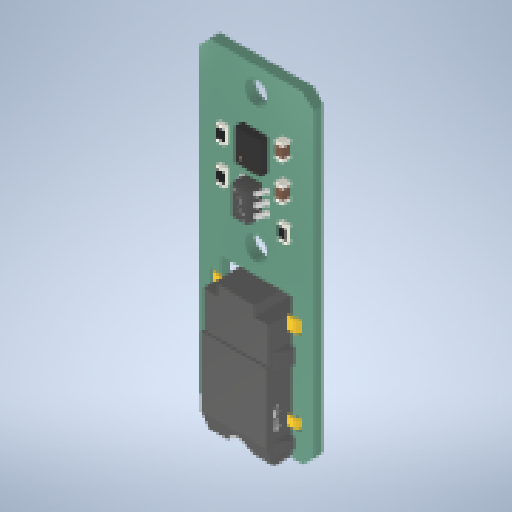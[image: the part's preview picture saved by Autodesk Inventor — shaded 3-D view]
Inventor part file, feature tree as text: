
AUTODESK INVENTOR PART (.ipt)
format: ipt  version: 2024 (Build 280153000, 153)  size: 1,688,064 bytes
history: native  units: in
note: dims shown in document units (in); Inventor stores cm internally (conversion verified against a paired STEP export)
features: move_body x2, direct_edit x1, chamfer x1
ambient origin geometry x8: Origin, YZ Plane, XZ Plane, XY Plane, X Axis, Y Axis, Z Axis, Center Point
bodies: Solid1 (feature_tree), Solid2 (feature_tree), Solid3 (feature_tree), Solid4 (feature_tree), Solid5 (feature_tree), Solid6 (feature_tree), Solid7 (feature_tree), Solid8 (feature_tree), Solid9 (feature_tree), Solid10 (feature_tree), Solid11 (feature_tree), Solid12 (feature_tree), Solid13 (feature_tree), Solid14 (feature_tree), Solid15 (feature_tree), Solid16 (feature_tree), Solid17 (feature_tree), Solid18 (feature_tree), Solid19 (feature_tree), Solid20 (feature_tree), Solid21 (feature_tree), Solid22 (feature_tree), Solid23 (feature_tree), Solid24 (feature_tree), Solid25 (feature_tree), Solid26 (feature_tree), Solid27 (feature_tree), Solid28 (feature_tree)
feature tree (4):
  direct_edit  "Direct Edit1"
  chamfer  "Chamfer1"  Distance=0.001in
  move_body  "Move1"
  move_body  "Move2"
